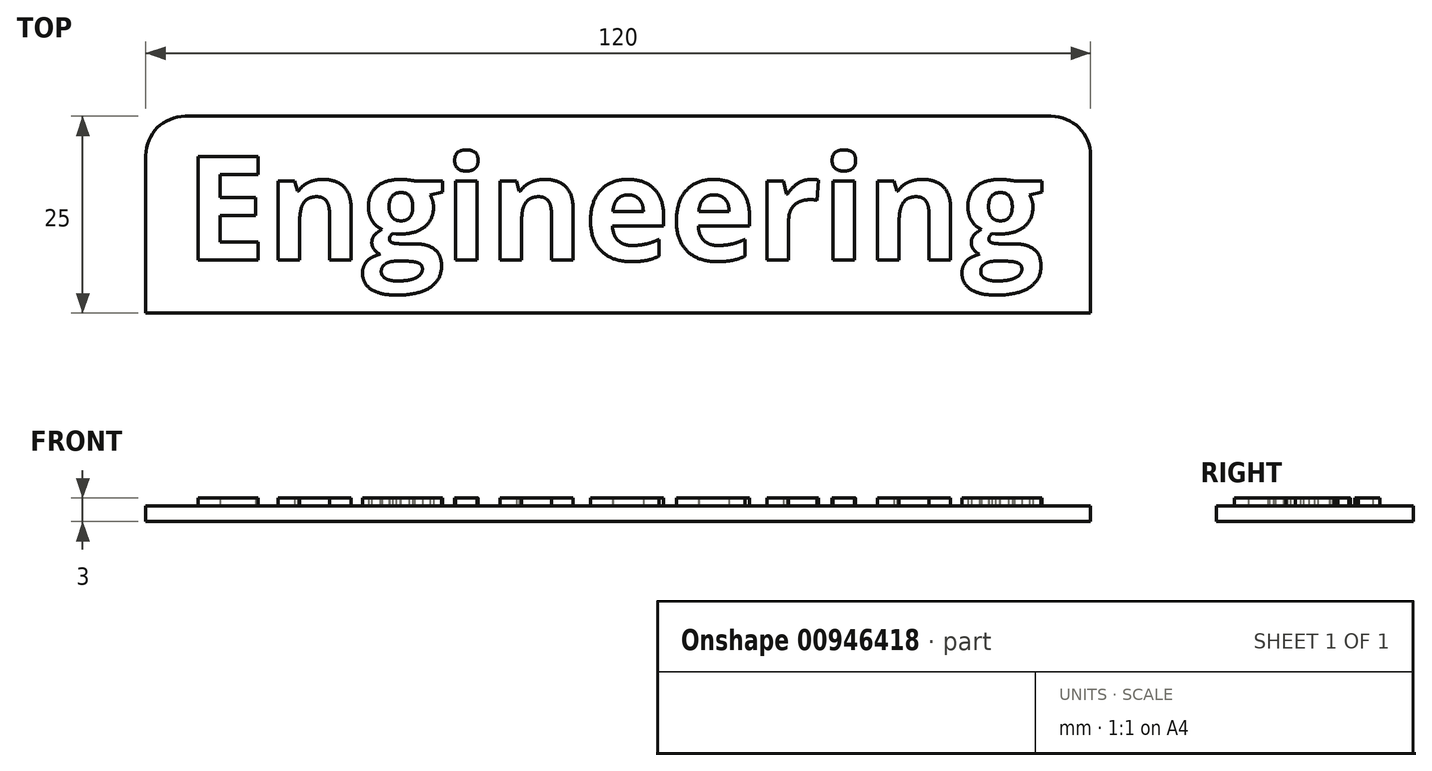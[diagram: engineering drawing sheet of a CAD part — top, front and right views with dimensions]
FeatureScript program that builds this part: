
annotation { "Feature Type Name" : "Feature", "Feature Type Description" : "" }
export const myFeature = defineFeature(function(context is Context, id is Id, definition is map)
    precondition{}
    {
        {
            var Q0;
            Q0=qCreatedBy(makeId("Top.planeOp"),FACE);
            var sketch = newSketch(context, id + "F0", { "sketchPlane" : qUnion([Q0])});
            skLineSegment(sketch, "E0.bottom", {"start": v(-60, 12.5) * mm, "end": v(60, 12.5) * mm});
            skLineSegment(sketch, "E0.top", {"start": v(-60, -12.5) * mm, "end": v(60, -12.5) * mm});
            skLineSegment(sketch, "E0.left", {"start": v(-60, 12.5) * mm, "end": v(-60, -12.5) * mm});
            skLineSegment(sketch, "E0.right", {"start": v(60, 12.5) * mm, "end": v(60, -12.5) * mm});
            skPoint(sketch, "E0.middle", {"position": v(0, 0) * mm});
            skSolve(sketch);
        }
        {
            var Q0;
            Q0=qSketchRegion(id+"F0",true);
            extrude(context, id + "F1", {"entities" : qUnion([Q0]), "depth" : 2 * mm, "offsetDistance" : 25 * mm});
        }
        {
            var Q0;
            Q0=makeQuery(id+"F1.opExtrude","CAP_FACE",FACE,{"disambiguationData":[OSD([sQuery(id+"F0.wireOp",EDGE,"E0.bottom"),sQuery(id+"F0.wireOp",EDGE,"E0.top"),sQuery(id+"F0.wireOp",EDGE,"E0.left"),sQuery(id+"F0.wireOp",EDGE,"E0.right")])],"isStart":false});
            var sketch = newSketch(context, id + "F2", { "sketchPlane" : qUnion([Q0])});
            skText(sketch, "E1", { "text": "Engineering\n", "fontName": "OpenSans-Bold.ttf"});
            const initialGuessF2  = {"E1": [-0.055, -0.00579, 1, 0, 0.01329]};
            skSetInitialGuess(sketch, initialGuessF2);
            skSolve(sketch);
        }
        {
            var Q0;
            Q0=qSketchRegion(id+"F2",true);
            extrude(context, id + "F3", {"entities" : qUnion([Q0]), "operationType" : NewBodyOperationType.ADD, "depth" : 1 * mm, "offsetDistance" : 25 * mm});
        }
        {
            var Q0;
            Q0=makeQuery(id+"F1.opExtrude","SWEPT_EDGE",EDGE,{"disambiguationData":[OSD([sQuery(id+"F0.wireOp",EDGE,"E0.bottom"),sQuery(id+"F0.wireOp",EDGE,"E0.left")])]});
            var Q1;
            Q1=makeQuery(id+"F1.opExtrude","SWEPT_EDGE",EDGE,{"disambiguationData":[OSD([sQuery(id+"F0.wireOp",EDGE,"E0.bottom"),sQuery(id+"F0.wireOp",EDGE,"E0.right")])]});
            fillet(context, id + "F4", {"entities" : qUnion([Q0, Q1]), "radius" : 5 * mm, "tangentPropagation" : true, "allowEdgeOverflow" : false});
        }
    });
